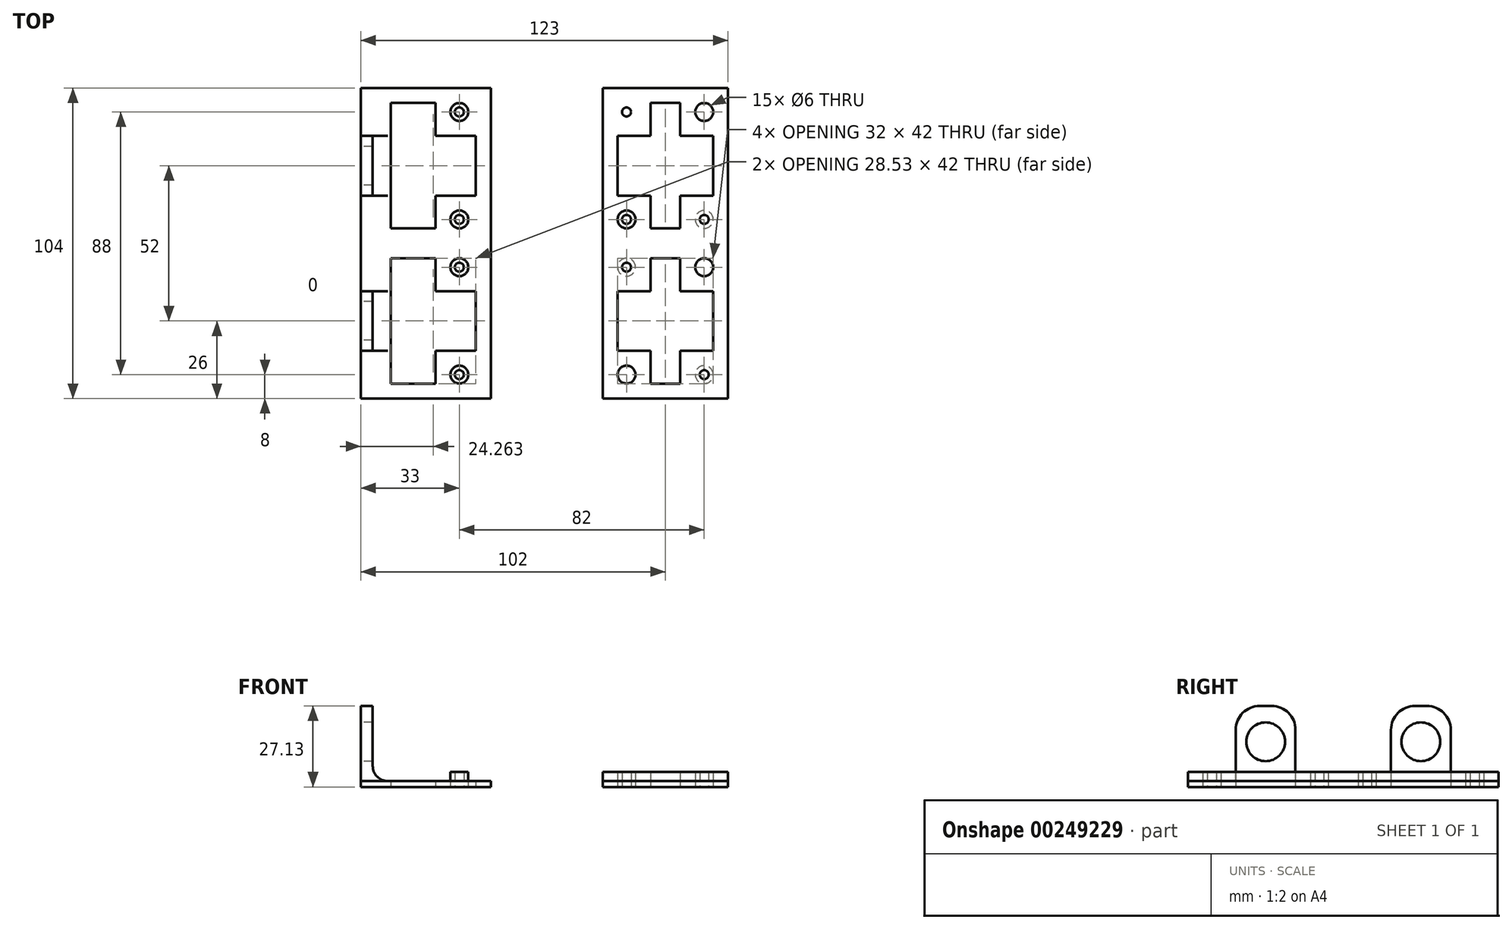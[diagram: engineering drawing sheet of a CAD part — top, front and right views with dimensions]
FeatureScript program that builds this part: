
annotation { "Feature Type Name" : "Feature", "Feature Type Description" : "" }
export const myFeature = defineFeature(function(context is Context, id is Id, definition is map)
    precondition{}
    {
        {
            var Q0;
            Q0=qCreatedBy(makeId("Top.planeOp"),FACE);
            var sketch = newSketch(context, id + "F0", { "sketchPlane" : qUnion([Q0])});
            skLineSegment(sketch, "E0.bottom", {"start": v(-10, 5) * mm, "end": v(-72, 5) * mm, "construction": true});
            skLineSegment(sketch, "E0.top", {"start": v(-10, 47) * mm, "end": v(-72, 47) * mm, "construction": true});
            skLineSegment(sketch, "E0.left", {"start": v(-10, 5) * mm, "end": v(-10, 47) * mm, "construction": true});
            skLineSegment(sketch, "E0.right", {"start": v(-72, 5) * mm, "end": v(-72, 47) * mm, "construction": true});
            skCircle(sketch, "E1", {"center": v(-13, 44) * mm, "radius": 1.5 * mm});
            skLineSegment(sketch, "E2", {"start": v(-41, 47) * mm, "end": v(-41, 5) * mm, "construction": true});
            skLineSegment(sketch, "E3", {"start": v(-72, 26) * mm, "end": v(-10, 26) * mm, "construction": true});
            skCircle(sketch, "E4.MirrorC", {"center": v(-13, 8) * mm, "radius": 1.5 * mm});
            skCircle(sketch, "E5.MirrorC", {"center": v(-69, 44) * mm, "radius": 1.5 * mm});
            skCircle(sketch, "E6.MirrorC", {"center": v(-69, 8) * mm, "radius": 1.5 * mm});
            skLineSegment(sketch, "E7", {"start": v(-102, -52) * mm, "end": v(-14, -52) * mm, "construction": true});
            skLineSegment(sketch, "E8", {"start": v(-102, 52) * mm, "end": v(-102, -52) * mm, "construction": true});
            skLineSegment(sketch, "E9", {"start": v(122, -62) * mm, "end": v(122, 62) * mm, "construction": true});
            skLineSegment(sketch, "E10.bottom", {"start": v(-102, 52) * mm, "end": v(-58.47, 52) * mm});
            skLineSegment(sketch, "E10.top", {"start": v(-102, -52) * mm, "end": v(-48, -52) * mm});
            skLineSegment(sketch, "E10.left", {"start": v(-102, 52) * mm, "end": v(-102, -52) * mm});
            skCircle(sketch, "E11", {"center": v(-13, 44) * mm, "radius": 3 * mm});
            skCircle(sketch, "E12.MirrorC", {"center": v(-13, 8) * mm, "radius": 3 * mm});
            skCircle(sketch, "E13.MirrorC", {"center": v(-69, 44) * mm, "radius": 3 * mm});
            skCircle(sketch, "E14.MirrorC", {"center": v(-69, 8) * mm, "radius": 3 * mm});
            skLineSegment(sketch, "E15", {"start": v(-58.47, 52) * mm, "end": v(-58.47, -52) * mm});
            skPoint(sketch, "E16.MirrorCS.end.orphan", {"position": v(102, -52) * mm});
            skPoint(sketch, "E16.MirrorCS.start.orphan", {"position": v(102, 52) * mm});
            skPoint(sketch, "E17.trimOffspring.end.orphan", {"position": v(48, -52) * mm});
            skLineSegment(sketch, "E18.MirrorCS", {"start": v(20, 52) * mm, "end": v(-23.53, 52) * mm});
            skLineSegment(sketch, "E19.MirrorCS", {"start": v(20, -52) * mm, "end": v(-68, -52) * mm, "construction": true});
            skLineSegment(sketch, "E20.bottom", {"start": v(-23.53, 52) * mm, "end": v(20, 52) * mm});
            skLineSegment(sketch, "E20.top", {"start": v(-24.76, -52) * mm, "end": v(20, -52) * mm});
            skCircle(sketch, "E21.MirrorC", {"center": v(13, 44) * mm, "radius": 3 * mm});
            skCircle(sketch, "E22.MirrorC", {"center": v(13, 44) * mm, "radius": 1.5 * mm});
            skCircle(sketch, "E23.MirrorC", {"center": v(13, 8) * mm, "radius": 3 * mm});
            skCircle(sketch, "E24.MirrorC", {"center": v(13, 8) * mm, "radius": 1.5 * mm});
            skLineSegment(sketch, "E25.MirrorCS", {"start": v(72, 5) * mm, "end": v(72, 47) * mm, "construction": true});
            skLineSegment(sketch, "E26.MirrorCS", {"start": v(10, 5) * mm, "end": v(10, 47) * mm, "construction": true});
            skLineSegment(sketch, "E27.MirrorCS", {"start": v(10, 5) * mm, "end": v(72, 5) * mm, "construction": true});
            skLineSegment(sketch, "E28.MirrorCS", {"start": v(10, 47) * mm, "end": v(72, 47) * mm, "construction": true});
            skLineSegment(sketch, "E29.bottom", {"start": v(-77, 47) * mm, "end": v(-92, 47) * mm});
            skLineSegment(sketch, "E29.top", {"start": v(-77, 5) * mm, "end": v(-92, 5) * mm});
            skLineSegment(sketch, "E29.left", {"start": v(-77, 47) * mm, "end": v(-77, 5) * mm});
            skLineSegment(sketch, "E29.right", {"start": v(-92, 47) * mm, "end": v(-92, 5) * mm});
            skLineSegment(sketch, "E30.bottom", {"start": v(-5, 47) * mm, "end": v(5, 47) * mm});
            skLineSegment(sketch, "E30.top", {"start": v(-5, 5) * mm, "end": v(5, 5) * mm});
            skLineSegment(sketch, "E30.left", {"start": v(-5, 47) * mm, "end": v(-5, 5) * mm});
            skLineSegment(sketch, "E30.right", {"start": v(5, 47) * mm, "end": v(5, 5) * mm});
            skCircle(sketch, "E31.MirrorC", {"center": v(-69, -8) * mm, "radius": 1.5 * mm});
            skCircle(sketch, "E32.MirrorC", {"center": v(-69, -8) * mm, "radius": 3 * mm});
            skCircle(sketch, "E33.MirrorC", {"center": v(-13, -8) * mm, "radius": 3 * mm});
            skCircle(sketch, "E34.MirrorC", {"center": v(-13, -8) * mm, "radius": 1.5 * mm});
            skCircle(sketch, "E35.MirrorC", {"center": v(13, -8) * mm, "radius": 3 * mm});
            skCircle(sketch, "E36.MirrorC", {"center": v(13, -8) * mm, "radius": 1.5 * mm});
            skCircle(sketch, "E37.MirrorC", {"center": v(13, -44) * mm, "radius": 3 * mm});
            skCircle(sketch, "E38.MirrorC", {"center": v(13, -44) * mm, "radius": 1.5 * mm});
            skCircle(sketch, "E39.MirrorC", {"center": v(-13, -44) * mm, "radius": 3 * mm});
            skCircle(sketch, "E40.MirrorC", {"center": v(-13, -44) * mm, "radius": 1.5 * mm});
            skCircle(sketch, "E41.MirrorC", {"center": v(-69, -44) * mm, "radius": 3 * mm});
            skCircle(sketch, "E42.MirrorC", {"center": v(-69, -44) * mm, "radius": 1.5 * mm});
            skLineSegment(sketch, "E43.MirrorCS", {"start": v(-10, -5) * mm, "end": v(-72, -5) * mm, "construction": true});
            skLineSegment(sketch, "E44.MirrorCS", {"start": v(-10, -47) * mm, "end": v(-72, -47) * mm, "construction": true});
            skLineSegment(sketch, "E45.MirrorCS", {"start": v(-72, -5) * mm, "end": v(-72, -47) * mm, "construction": true});
            skLineSegment(sketch, "E46.MirrorCS", {"start": v(-10, -5) * mm, "end": v(-10, -47) * mm, "construction": true});
            skLineSegment(sketch, "E47.MirrorCS", {"start": v(10, -5) * mm, "end": v(10, -47) * mm, "construction": true});
            skLineSegment(sketch, "E48.MirrorCS", {"start": v(10, -5) * mm, "end": v(72, -5) * mm, "construction": true});
            skLineSegment(sketch, "E49.MirrorCS", {"start": v(10, -47) * mm, "end": v(72, -47) * mm, "construction": true});
            skLineSegment(sketch, "E50.MirrorCS", {"start": v(72, -5) * mm, "end": v(72, -47) * mm, "construction": true});
            skLineSegment(sketch, "E51.MirrorCS", {"start": v(-92, -47) * mm, "end": v(-92, -5) * mm});
            skLineSegment(sketch, "E52.MirrorCS", {"start": v(-77, -47) * mm, "end": v(-92, -47) * mm});
            skLineSegment(sketch, "E53.MirrorCS", {"start": v(-77, -47) * mm, "end": v(-77, -5) * mm});
            skLineSegment(sketch, "E54.MirrorCS", {"start": v(-77, -5) * mm, "end": v(-92, -5) * mm});
            skLineSegment(sketch, "E55.MirrorCS", {"start": v(-5, -5) * mm, "end": v(5, -5) * mm});
            skLineSegment(sketch, "E56.MirrorCS", {"start": v(5, -47) * mm, "end": v(5, -5) * mm});
            skLineSegment(sketch, "E57.MirrorCS", {"start": v(-5, -47) * mm, "end": v(-5, -5) * mm});
            skLineSegment(sketch, "E58.MirrorCS", {"start": v(-5, -47) * mm, "end": v(5, -47) * mm});
            skLineSegment(sketch, "E59.bottom", {"start": v(-80.53, 36) * mm, "end": v(-63.47, 36) * mm});
            skLineSegment(sketch, "E59.top", {"start": v(-80.53, 16) * mm, "end": v(-63.47, 16) * mm});
            skLineSegment(sketch, "E59.left", {"start": v(-80.53, 36) * mm, "end": v(-80.53, 16) * mm});
            skLineSegment(sketch, "E59.right", {"start": v(-63.47, 36) * mm, "end": v(-63.47, 16) * mm});
            skPoint(sketch, "E59.middle", {"position": v(-72, 26) * mm});
            skLineSegment(sketch, "E60.MirrorCS", {"start": v(-63.47, -36) * mm, "end": v(-63.47, -16) * mm});
            skLineSegment(sketch, "E61.MirrorCS", {"start": v(-80.53, -16) * mm, "end": v(-63.47, -16) * mm});
            skLineSegment(sketch, "E62.MirrorCS", {"start": v(-80.53, -36) * mm, "end": v(-80.53, -16) * mm});
            skLineSegment(sketch, "E63.MirrorCS", {"start": v(-80.53, -36) * mm, "end": v(-63.47, -36) * mm});
            skLineSegment(sketch, "E64", {"start": v(-10, 26) * mm, "end": v(10, 26) * mm, "construction": true});
            skLineSegment(sketch, "E65", {"start": v(0, 47) * mm, "end": v(0, 5) * mm, "construction": true});
            skLineSegment(sketch, "E66.bottom", {"start": v(-16, 36) * mm, "end": v(16, 36) * mm});
            skLineSegment(sketch, "E66.top", {"start": v(-16, 16) * mm, "end": v(16, 16) * mm});
            skLineSegment(sketch, "E66.left", {"start": v(-16, 36) * mm, "end": v(-16, 16) * mm});
            skLineSegment(sketch, "E66.right", {"start": v(16, 36) * mm, "end": v(16, 16) * mm});
            skPoint(sketch, "E66.middle", {"position": v(0, 26) * mm});
            skLineSegment(sketch, "E67.bottom", {"start": v(20, 52) * mm, "end": v(-20, 52) * mm});
            skLineSegment(sketch, "E67.top", {"start": v(20, -52) * mm, "end": v(-20, -52) * mm});
            skPoint(sketch, "E67.middle", {"position": v(0, 0) * mm});
            skPoint(sketch, "E68.trimOffspring.end.orphan", {"position": v(-23.53, -52) * mm});
            skLineSegment(sketch, "E69.bottom", {"start": v(21, 52) * mm, "end": v(-21, 52) * mm});
            skLineSegment(sketch, "E69.top", {"start": v(21, -52) * mm, "end": v(-21, -52) * mm});
            skLineSegment(sketch, "E69.left", {"start": v(21, 52) * mm, "end": v(21, -52) * mm});
            skLineSegment(sketch, "E69.right", {"start": v(-21, 52) * mm, "end": v(-21, -52) * mm});
            skLineSegment(sketch, "E70.MirrorCS", {"start": v(16, -36) * mm, "end": v(16, -16) * mm});
            skLineSegment(sketch, "E71.MirrorCS", {"start": v(-16, -36) * mm, "end": v(16, -36) * mm});
            skLineSegment(sketch, "E72.MirrorCS", {"start": v(-16, -36) * mm, "end": v(-16, -16) * mm});
            skLineSegment(sketch, "E73.MirrorCS", {"start": v(-16, -16) * mm, "end": v(16, -16) * mm});
            skSolve(sketch);
        }
        {
            var Q0;
            Q0=makeQuery(id+"F0.imprint","IMPRINT",FACE,{"disambiguationData":[TD([[makeQuery(id+"F0.imprint","IMPRINT",EDGE,{"derivedFrom":sQuery(id+"F0.wireOp",EDGE,"E4.MirrorC")}),1.0]])]});
            var Q1;
            Q1=makeQuery(id+"F0.imprint","IMPRINT",FACE,{"disambiguationData":[TD([[makeQuery(id+"F0.imprint","IMPRINT",EDGE,{"derivedFrom":sQuery(id+"F0.wireOp",EDGE,"E10.bottom")}),-1.0]])]});
            var Q2;
            Q2=makeQuery(id+"F0.imprint","IMPRINT",FACE,{"disambiguationData":[TD([[makeQuery(id+"F0.imprint","IMPRINT",EDGE,{"derivedFrom":sQuery(id+"F0.wireOp",EDGE,"E1")}),-1.0]])]});
            var Q3;
            Q3=makeQuery(id+"F0.imprint","IMPRINT",FACE,{"disambiguationData":[TD([[makeQuery(id+"F0.imprint","IMPRINT",EDGE,{"derivedFrom":sQuery(id+"F0.wireOp",EDGE,"E4.MirrorC")}),1.0]])]});
            var Q4;
            Q4=makeQuery(id+"F0.imprint","IMPRINT",FACE,{"disambiguationData":[TD([[makeQuery(id+"F0.imprint","IMPRINT",EDGE,{"derivedFrom":sQuery(id+"F0.wireOp",EDGE,"E11")}),-1.0]])]});
            extrude(context, id + "F1", {"entities" : qUnion([Q0, Q1, Q2, Q3, Q4]), "depth" : 2 * mm});
        }
        {
            var Q0;
            Q0=makeQuery(id+"F0.imprint","IMPRINT",FACE,{"disambiguationData":[TD([[makeQuery(id+"F0.imprint","IMPRINT",EDGE,{"derivedFrom":sQuery(id+"F0.wireOp",EDGE,"E5.MirrorC")}),1.0]])]});
            var Q1;
            Q1=makeQuery(id+"F0.imprint","IMPRINT",FACE,{"disambiguationData":[TD([[makeQuery(id+"F0.imprint","IMPRINT",EDGE,{"derivedFrom":sQuery(id+"F0.wireOp",EDGE,"E6.MirrorC")}),-1.0]])]});
            var Q2;
            Q2=makeQuery(id+"F0.imprint","IMPRINT",FACE,{"disambiguationData":[TD([[makeQuery(id+"F0.imprint","IMPRINT",EDGE,{"derivedFrom":sQuery(id+"F0.wireOp",EDGE,"E4.MirrorC")}),1.0]])]});
            var Q3;
            Q3=makeQuery(id+"F0.imprint","IMPRINT",FACE,{"disambiguationData":[TD([[makeQuery(id+"F0.imprint","IMPRINT",EDGE,{"derivedFrom":sQuery(id+"F0.wireOp",EDGE,"E1")}),-1.0]])]});
            var Q4;
            Q4=makeQuery(id+"F0.imprint","IMPRINT",FACE,{"disambiguationData":[TD([[makeQuery(id+"F0.imprint","IMPRINT",EDGE,{"derivedFrom":sQuery(id+"F0.wireOp",EDGE,"54afa595-782a-44cc-b530-174a9ed369d55.MirrorC")}),1.0]])]});
            var Q5;
            Q5=makeQuery(id+"F0.imprint","IMPRINT",FACE,{"disambiguationData":[TD([[makeQuery(id+"F0.imprint","IMPRINT",EDGE,{"derivedFrom":sQuery(id+"F0.wireOp",EDGE,"54afa595-782a-44cc-b530-174a9ed369d57.MirrorC")}),-1.0]])]});
            var Q6;
            Q6=makeQuery(id+"F0.imprint","IMPRINT",FACE,{"disambiguationData":[TD([[makeQuery(id+"F0.imprint","IMPRINT",EDGE,{"derivedFrom":sQuery(id+"F0.wireOp",EDGE,"25e94151-ceff-47d8-9de0-a60d4fc2466f5.MirrorC")}),1.0]])]});
            var Q7;
            Q7=makeQuery(id+"F0.imprint","IMPRINT",FACE,{"disambiguationData":[TD([[makeQuery(id+"F0.imprint","IMPRINT",EDGE,{"derivedFrom":sQuery(id+"F0.wireOp",EDGE,"25e94151-ceff-47d8-9de0-a60d4fc2466f7.MirrorC")}),-1.0]])]});
            var Q8;
            Q8=makeQuery(id+"F0.imprint","IMPRINT",FACE,{"disambiguationData":[TD([[makeQuery(id+"F0.imprint","IMPRINT",EDGE,{"derivedFrom":sQuery(id+"F0.wireOp",EDGE,"54afa595-782a-44cc-b530-174a9ed369d59.MirrorC")}),-1.0]])]});
            var Q9;
            Q9=makeQuery(id+"F0.imprint","IMPRINT",FACE,{"disambiguationData":[TD([[makeQuery(id+"F0.imprint","IMPRINT",EDGE,{"derivedFrom":sQuery(id+"F0.wireOp",EDGE,"25e94151-ceff-47d8-9de0-a60d4fc2466f19.MirrorC")}),1.0]])]});
            var Q10;
            Q10=makeQuery(id+"F0.imprint","IMPRINT",FACE,{"disambiguationData":[TD([[makeQuery(id+"F0.imprint","IMPRINT",EDGE,{"derivedFrom":sQuery(id+"F0.wireOp",EDGE,"25e94151-ceff-47d8-9de0-a60d4fc2466f14.MirrorC")}),-1.0]])]});
            var Q11;
            Q11=makeQuery(id+"F0.imprint","IMPRINT",FACE,{"disambiguationData":[TD([[makeQuery(id+"F0.imprint","IMPRINT",EDGE,{"derivedFrom":sQuery(id+"F0.wireOp",EDGE,"25e94151-ceff-47d8-9de0-a60d4fc2466f6.MirrorC")}),-1.0]])]});
            var Q12;
            Q12=makeQuery(id+"F0.imprint","IMPRINT",FACE,{"disambiguationData":[TD([[makeQuery(id+"F0.imprint","IMPRINT",EDGE,{"derivedFrom":sQuery(id+"F0.wireOp",EDGE,"25e94151-ceff-47d8-9de0-a60d4fc2466f11.MirrorC")}),1.0]])]});
            var Q13;
            Q13=makeQuery(id+"F0.imprint","IMPRINT",FACE,{"disambiguationData":[TD([[makeQuery(id+"F0.imprint","IMPRINT",EDGE,{"derivedFrom":sQuery(id+"F0.wireOp",EDGE,"25e94151-ceff-47d8-9de0-a60d4fc2466f16.MirrorC")}),1.0]])]});
            var Q14;
            Q14=makeQuery(id+"F0.imprint","IMPRINT",FACE,{"disambiguationData":[TD([[makeQuery(id+"F0.imprint","IMPRINT",EDGE,{"derivedFrom":sQuery(id+"F0.wireOp",EDGE,"54afa595-782a-44cc-b530-174a9ed369d53.MirrorC")}),1.0]])]});
            var Q15;
            Q15=makeQuery(id+"F0.imprint","IMPRINT",FACE,{"disambiguationData":[TD([[makeQuery(id+"F0.imprint","IMPRINT",EDGE,{"derivedFrom":sQuery(id+"F0.wireOp",EDGE,"25e94151-ceff-47d8-9de0-a60d4fc2466f17.MirrorC")}),-1.0]])]});
            var Q16;
            Q16=makeQuery(id+"F0.imprint","IMPRINT",FACE,{"disambiguationData":[TD([[makeQuery(id+"F0.imprint","IMPRINT",EDGE,{"derivedFrom":sQuery(id+"F0.wireOp",EDGE,"E21.MirrorC")}),-1.0]])]});
            var Q17;
            Q17=makeQuery(id+"F0.imprint","IMPRINT",FACE,{"disambiguationData":[TD([[makeQuery(id+"F0.imprint","IMPRINT",EDGE,{"derivedFrom":sQuery(id+"F0.wireOp",EDGE,"E23.MirrorC")}),1.0]])]});
            var Q18;
            Q18=makeQuery(id+"F0.imprint","IMPRINT",FACE,{"disambiguationData":[TD([[makeQuery(id+"F0.imprint","IMPRINT",EDGE,{"derivedFrom":sQuery(id+"F0.wireOp",EDGE,"E31.MirrorC")}),1.0]])]});
            var Q19;
            Q19=makeQuery(id+"F0.imprint","IMPRINT",FACE,{"disambiguationData":[TD([[makeQuery(id+"F0.imprint","IMPRINT",EDGE,{"derivedFrom":sQuery(id+"F0.wireOp",EDGE,"E33.MirrorC")}),1.0]])]});
            var Q20;
            Q20=makeQuery(id+"F0.imprint","IMPRINT",FACE,{"disambiguationData":[TD([[makeQuery(id+"F0.imprint","IMPRINT",EDGE,{"derivedFrom":sQuery(id+"F0.wireOp",EDGE,"E35.MirrorC")}),-1.0]])]});
            var Q21;
            Q21=makeQuery(id+"F0.imprint","IMPRINT",FACE,{"disambiguationData":[TD([[makeQuery(id+"F0.imprint","IMPRINT",EDGE,{"derivedFrom":sQuery(id+"F0.wireOp",EDGE,"E41.MirrorC")}),1.0]])]});
            var Q22;
            Q22=makeQuery(id+"F0.imprint","IMPRINT",FACE,{"disambiguationData":[TD([[makeQuery(id+"F0.imprint","IMPRINT",EDGE,{"derivedFrom":sQuery(id+"F0.wireOp",EDGE,"E39.MirrorC")}),-1.0]])]});
            var Q23;
            Q23=makeQuery(id+"F0.imprint","IMPRINT",FACE,{"disambiguationData":[TD([[makeQuery(id+"F0.imprint","IMPRINT",EDGE,{"derivedFrom":sQuery(id+"F0.wireOp",EDGE,"E37.MirrorC")}),1.0]])]});
            extrude(context, id + "F2", {"entities" : qUnion([Q0, Q1, Q2, Q3, Q4, Q5, Q6, Q7, Q8, Q9, Q10, Q11, Q12, Q13, Q14, Q15, Q16, Q17, Q18, Q19, Q20, Q21, Q22, Q23]), "depth" : 5 * mm});
        }
        {
            var Q0;
            Q0=qCreatedBy(makeId("Right.planeOp"),FACE);
            var sketch = newSketch(context, id + "F3", { "sketchPlane" : qUnion([Q0])});
            skLineSegment(sketch, "E74.0", {"start": v(52, 2) * mm, "end": v(52, 0) * mm, "construction": true});
            skLineSegment(sketch, "E75.0", {"start": v(52, 0) * mm, "end": v(37.33, 0) * mm, "construction": true});
            skPoint(sketch, "E76.0", {"position": v(0, 0) * mm});
            skLineSegment(sketch, "E77", {"start": v(0, 0) * mm, "end": v(0, 14.94) * mm, "construction": true});
            skLineSegment(sketch, "E78.bottom", {"start": v(31, 0) * mm, "end": v(37.33, 0) * mm});
            skLineSegment(sketch, "E79", {"start": v(36, 28.6) * mm, "end": v(19, 0) * mm, "construction": true});
            skLineSegment(sketch, "E80", {"start": v(14.66, 30.25) * mm, "end": v(37.33, 0) * mm, "construction": true});
            skCircle(sketch, "E81", {"center": v(26, 15.13) * mm, "radius": 6.5 * mm});
            skPoint(sketch, "E82.MirrorCS.start.orphan", {"position": v(31, 30) * mm});
            skPoint(sketch, "E83.MirrorCS.end.orphan", {"position": v(19, 30) * mm});
            skLineSegment(sketch, "E84.trimOffspring", {"start": v(19, 0) * mm, "end": v(-52, 0) * mm, "construction": true});
            skLineSegment(sketch, "E85.bottom", {"start": v(36, 0) * mm, "end": v(16, 0.47) * mm});
            skLineSegment(sketch, "E85.left", {"start": v(36, 0) * mm, "end": v(36, 27.13) * mm});
            skLineSegment(sketch, "E85.right", {"start": v(16, 0.47) * mm, "end": v(16, 28.47) * mm});
            skLineSegment(sketch, "E86", {"start": v(36, 27.13) * mm, "end": v(16, 27.13) * mm});
            skPoint(sketch, "E87.orphan", {"position": v(36, 29.78) * mm});
            skPoint(sketch, "E88.orphan", {"position": v(16, 30.25) * mm});
            skCircle(sketch, "E89.MirrorC", {"center": v(-26, 15.13) * mm, "radius": 6.5 * mm});
            skLineSegment(sketch, "E90.MirrorCS", {"start": v(-36, 27.13) * mm, "end": v(-16, 27.13) * mm});
            skLineSegment(sketch, "E91.MirrorCS", {"start": v(-16, 0.47) * mm, "end": v(-16, 28.47) * mm});
            skLineSegment(sketch, "E92.MirrorCS", {"start": v(-36, 0) * mm, "end": v(-36, 27.13) * mm});
            skLineSegment(sketch, "E93.MirrorCS", {"start": v(-36, 0) * mm, "end": v(-16, 0.47) * mm});
            skLineSegment(sketch, "E94", {"start": v(41, 0) * mm, "end": v(41, 5) * mm});
            skLineSegment(sketch, "E95", {"start": v(11, 5) * mm, "end": v(11, 0) * mm});
            skSolve(sketch);
        }
        {
            var Q0;
            Q0=makeQuery(id+"F1.opExtrude","SWEPT_FACE",FACE,{"disambiguationData":[OSD([sQuery(id+"F0.wireOp",EDGE,"E10.left")])]});
            var sketch = newSketch(context, id + "F4", { "sketchPlane" : qUnion([Q0])});
            skCircle(sketch, "E96.0", {"center": v(-26, 15.13) * mm, "radius": 6.5 * mm});
            skLineSegment(sketch, "E97.0", {"start": v(-36, 27.13) * mm, "end": v(-16, 27.13) * mm});
            skLineSegment(sketch, "E98.0", {"start": v(-16, 0.47) * mm, "end": v(-16, 28.47) * mm});
            skLineSegment(sketch, "E99.0", {"start": v(-36, 0) * mm, "end": v(-36, 27.13) * mm});
            skLineSegment(sketch, "E100.0.0", {"start": v(-16, 0.47) * mm, "end": v(-36, 0) * mm});
            skLineSegment(sketch, "E100.0.3", {"start": v(-16, 27.13) * mm, "end": v(-16, 0.47) * mm});
            skLineSegment(sketch, "E101.0.0", {"start": v(36, 0) * mm, "end": v(16, 0.47) * mm});
            skLineSegment(sketch, "E101.0.1", {"start": v(16, 0.47) * mm, "end": v(16, 27.13) * mm});
            skLineSegment(sketch, "E101.0.2", {"start": v(16, 27.13) * mm, "end": v(36, 27.13) * mm});
            skLineSegment(sketch, "E101.0.3", {"start": v(36, 27.13) * mm, "end": v(36, 0) * mm});
            skCircle(sketch, "E102.0", {"center": v(26, 15.13) * mm, "radius": 6.5 * mm});
            skSolve(sketch);
        }
        {
            var Q0;
            Q0 = qSketchRegion(id + "F4", true);
            extrude(context, id + "F5", {"entities" : qUnion([Q0]), "operationType" : NewBodyOperationType.ADD, "oppositeDirection" : true, "depth" : 4 * mm});
        }
        {
            var Q0;
            Q0=makeQuery(id+"F5.boolean.opBoolean","INTERSECT",EDGE,{"derivedFrom":[makeQuery(id+"F1.opExtrude","CAP_FACE",FACE,{"disambiguationData":[OSD([sQuery(id+"F0.wireOp",EDGE,"E10.bottom"),sQuery(id+"F0.wireOp",EDGE,"E10.top"),sQuery(id+"F0.wireOp",EDGE,"E10.left"),sQuery(id+"F0.wireOp",EDGE,"E13.MirrorC"),sQuery(id+"F0.wireOp",EDGE,"E14.MirrorC"),sQuery(id+"F0.wireOp",EDGE,"E15")])],"isStart":false}),makeQuery(id+"F5.opExtrude","CAP_FACE",FACE,{"disambiguationData":[OSD([sQuery(id+"F4.wireOp",EDGE,"E96.0"),sQuery(id+"F4.wireOp",EDGE,"E100.0.0"),sQuery(id+"F4.wireOp",EDGE,"E99.0"),sQuery(id+"F4.wireOp",EDGE,"E97.0"),sQuery(id+"F4.wireOp",EDGE,"E100.0.3")])],"isStart":false})]});
            var Q1;
            Q1=makeQuery(id+"F5.boolean.opBoolean","INTERSECT",EDGE,{"derivedFrom":[makeQuery(id+"F1.opExtrude","CAP_FACE",FACE,{"disambiguationData":[OSD([sQuery(id+"F0.wireOp",EDGE,"E10.bottom"),sQuery(id+"F0.wireOp",EDGE,"E10.top"),sQuery(id+"F0.wireOp",EDGE,"E10.left"),sQuery(id+"F0.wireOp",EDGE,"E13.MirrorC"),sQuery(id+"F0.wireOp",EDGE,"E14.MirrorC"),sQuery(id+"F0.wireOp",EDGE,"E15")])],"isStart":false}),makeQuery(id+"F5.opExtrude","CAP_FACE",FACE,{"disambiguationData":[OSD([sQuery(id+"F4.wireOp",EDGE,"E101.0.0"),sQuery(id+"F4.wireOp",EDGE,"E101.0.1"),sQuery(id+"F4.wireOp",EDGE,"E101.0.2"),sQuery(id+"F4.wireOp",EDGE,"E101.0.3"),sQuery(id+"F4.wireOp",EDGE,"E102.0")])],"isStart":false})]});
            fillet(context, id + "F6", {"entities" : qUnion([Q0, Q1]), "radius" : 5 * mm, "tangentPropagation" : true, "allowEdgeOverflow" : false});
        }
        {
            var Q0;
            Q0=makeQuery(id+"F5.opExtrude","SWEPT_EDGE",EDGE,{"disambiguationData":[OSD([sQuery(id+"F4.wireOp",EDGE,"E99.0"),sQuery(id+"F4.wireOp",EDGE,"E97.0")])]});
            var Q1;
            Q1=makeQuery(id+"F5.opExtrude","SWEPT_EDGE",EDGE,{"disambiguationData":[OSD([sQuery(id+"F4.wireOp",EDGE,"E101.0.1"),sQuery(id+"F4.wireOp",EDGE,"E101.0.2")])]});
            var Q2;
            Q2=makeQuery(id+"F5.opExtrude","SWEPT_EDGE",EDGE,{"disambiguationData":[OSD([sQuery(id+"F4.wireOp",EDGE,"E97.0"),sQuery(id+"F4.wireOp",EDGE,"E100.0.3")])]});
            var Q3;
            Q3=makeQuery(id+"F5.opExtrude","SWEPT_EDGE",EDGE,{"disambiguationData":[OSD([sQuery(id+"F4.wireOp",EDGE,"E101.0.2"),sQuery(id+"F4.wireOp",EDGE,"E101.0.3")])]});
            fillet(context, id + "F7", {"entities" : qUnion([Q0, Q1, Q2, Q3]), "radius" : 8 * mm, "tangentPropagation" : true, "allowEdgeOverflow" : false});
        }
    });
